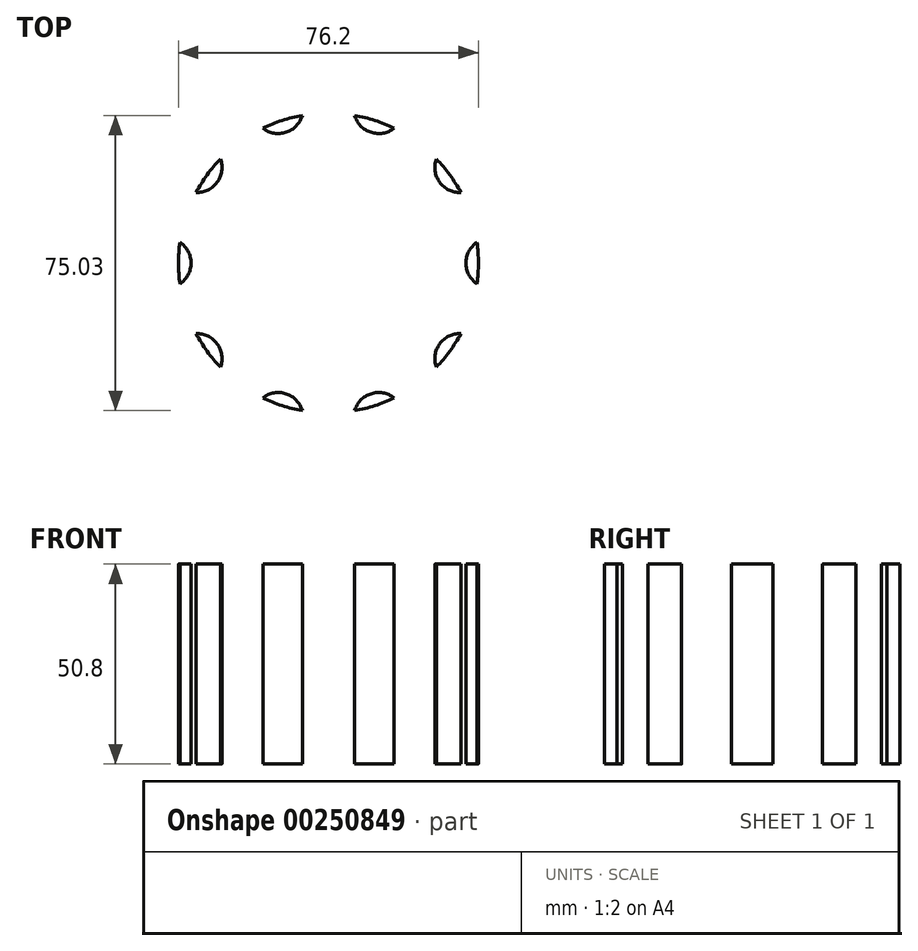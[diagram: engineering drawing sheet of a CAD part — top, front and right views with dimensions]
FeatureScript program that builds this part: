
annotation { "Feature Type Name" : "Feature", "Feature Type Description" : "" }
export const myFeature = defineFeature(function(context is Context, id is Id, definition is map)
    precondition{}
    {
        {
            var Q0;
            Q0=qCreatedBy(makeId("Top.planeOp"),FACE);
            var sketch = newSketch(context, id + "F0", { "sketchPlane" : qUnion([Q0])});
            skCircle(sketch, "E0", {"center": v(-2.67, -0.87) * mm, "radius": 38.1 * mm});
            skCircle(sketch, "E1", {"center": v(38.6, -0.87) * mm, "radius": 6.35 * mm});
            skCircle(sketch, "E2.1.0", {"center": v(30.73, -25.13) * mm, "radius": 6.35 * mm});
            skCircle(sketch, "E2.2.0", {"center": v(10.09, -40.12) * mm, "radius": 6.35 * mm});
            skCircle(sketch, "E2.3.0", {"center": v(-15.42, -40.12) * mm, "radius": 6.35 * mm});
            skCircle(sketch, "E2.4.0", {"center": v(-36.06, -25.13) * mm, "radius": 6.35 * mm});
            skCircle(sketch, "E2.5.0", {"center": v(-43.94, -0.87) * mm, "radius": 6.35 * mm});
            skCircle(sketch, "E2.6.0", {"center": v(-36.06, 23.4) * mm, "radius": 6.35 * mm});
            skCircle(sketch, "E2.7.0", {"center": v(-15.42, 38.39) * mm, "radius": 6.35 * mm});
            skCircle(sketch, "E2.8.0", {"center": v(10.09, 38.39) * mm, "radius": 6.35 * mm});
            skCircle(sketch, "E2.9.0", {"center": v(30.73, 23.4) * mm, "radius": 6.35 * mm});
            skLineSegment(sketch, "E2.anchor1", {"start": v(-2.67, -0.87) * mm, "end": v(38.6, -0.87) * mm, "construction": true});
            skLineSegment(sketch, "E2.anchor2", {"start": v(-2.67, -0.87) * mm, "end": v(30.73, 23.4) * mm, "construction": true});
            skSolve(sketch);
        }
        {
            var Q0;
            {var subQ0=sQuery(id+"F0.wireOp",EDGE,"E2.7.0");var subQ1=sQuery(id+"F0.wireOp",EDGE,"E0");var subQ2=makeQuery(id+"F0.imprint","INTERSECT",VERTEX,{"disambiguationData":[OD(0.0)],"derivedFrom":[subQ1,subQ0]});Q0=makeQuery(id+"F0.imprint","IMPRINT",FACE,{"disambiguationData":[TD([[makeQuery(id+"F0.imprint","IMPRINT",EDGE,{"disambiguationData":[TD([[subQ2,-1.0]])],"derivedFrom":subQ1}),1.0]])]});}
            var Q1;
            {var subQ0=sQuery(id+"F0.wireOp",EDGE,"E2.6.0");var subQ1=sQuery(id+"F0.wireOp",EDGE,"E0");var subQ2=makeQuery(id+"F0.imprint","INTERSECT",VERTEX,{"disambiguationData":[OD(0.0)],"derivedFrom":[subQ1,subQ0]});Q1=makeQuery(id+"F0.imprint","IMPRINT",FACE,{"disambiguationData":[TD([[makeQuery(id+"F0.imprint","IMPRINT",EDGE,{"disambiguationData":[TD([[subQ2,-1.0]])],"derivedFrom":subQ1}),1.0]])]});}
            var Q2;
            {var subQ0=sQuery(id+"F0.wireOp",EDGE,"E2.5.0");var subQ1=sQuery(id+"F0.wireOp",EDGE,"E0");var subQ2=makeQuery(id+"F0.imprint","INTERSECT",VERTEX,{"disambiguationData":[OD(0.0)],"derivedFrom":[subQ1,subQ0]});Q2=makeQuery(id+"F0.imprint","IMPRINT",FACE,{"disambiguationData":[TD([[makeQuery(id+"F0.imprint","IMPRINT",EDGE,{"disambiguationData":[TD([[subQ2,-1.0]])],"derivedFrom":subQ1}),1.0]])]});}
            var Q3;
            {var subQ0=sQuery(id+"F0.wireOp",EDGE,"E2.8.0");var subQ1=sQuery(id+"F0.wireOp",EDGE,"E0");var subQ2=makeQuery(id+"F0.imprint","INTERSECT",VERTEX,{"disambiguationData":[OD(0.0)],"derivedFrom":[subQ1,subQ0]});Q3=makeQuery(id+"F0.imprint","IMPRINT",FACE,{"disambiguationData":[TD([[makeQuery(id+"F0.imprint","IMPRINT",EDGE,{"disambiguationData":[TD([[subQ2,-1.0]])],"derivedFrom":subQ1}),1.0]])]});}
            var Q4;
            {var subQ0=sQuery(id+"F0.wireOp",EDGE,"E2.9.0");var subQ1=sQuery(id+"F0.wireOp",EDGE,"E0");var subQ2=makeQuery(id+"F0.imprint","INTERSECT",VERTEX,{"disambiguationData":[OD(0.0)],"derivedFrom":[subQ1,subQ0]});Q4=makeQuery(id+"F0.imprint","IMPRINT",FACE,{"disambiguationData":[TD([[makeQuery(id+"F0.imprint","IMPRINT",EDGE,{"disambiguationData":[TD([[subQ2,-1.0]])],"derivedFrom":subQ1}),1.0]])]});}
            var Q5;
            {var subQ0=sQuery(id+"F0.wireOp",EDGE,"E1");var subQ1=sQuery(id+"F0.wireOp",EDGE,"E0");var subQ2=makeQuery(id+"F0.imprint","INTERSECT",VERTEX,{"disambiguationData":[OD(0.0)],"derivedFrom":[subQ1,subQ0]});Q5=makeQuery(id+"F0.imprint","IMPRINT",FACE,{"disambiguationData":[TD([[makeQuery(id+"F0.imprint","IMPRINT",EDGE,{"disambiguationData":[TD([[subQ2,1.0]])],"derivedFrom":subQ1}),1.0]])]});}
            var Q6;
            {var subQ0=sQuery(id+"F0.wireOp",EDGE,"E2.1.0");var subQ1=sQuery(id+"F0.wireOp",EDGE,"E0");var subQ2=makeQuery(id+"F0.imprint","INTERSECT",VERTEX,{"disambiguationData":[OD(0.0)],"derivedFrom":[subQ1,subQ0]});Q6=makeQuery(id+"F0.imprint","IMPRINT",FACE,{"disambiguationData":[TD([[makeQuery(id+"F0.imprint","IMPRINT",EDGE,{"disambiguationData":[TD([[subQ2,-1.0]])],"derivedFrom":subQ1}),1.0]])]});}
            var Q7;
            {var subQ0=sQuery(id+"F0.wireOp",EDGE,"E2.2.0");var subQ1=sQuery(id+"F0.wireOp",EDGE,"E0");var subQ2=makeQuery(id+"F0.imprint","INTERSECT",VERTEX,{"disambiguationData":[OD(0.0)],"derivedFrom":[subQ1,subQ0]});Q7=makeQuery(id+"F0.imprint","IMPRINT",FACE,{"disambiguationData":[TD([[makeQuery(id+"F0.imprint","IMPRINT",EDGE,{"disambiguationData":[TD([[subQ2,-1.0]])],"derivedFrom":subQ1}),1.0]])]});}
            var Q8;
            {var subQ0=sQuery(id+"F0.wireOp",EDGE,"E2.3.0");var subQ1=sQuery(id+"F0.wireOp",EDGE,"E0");var subQ2=makeQuery(id+"F0.imprint","INTERSECT",VERTEX,{"disambiguationData":[OD(0.0)],"derivedFrom":[subQ1,subQ0]});Q8=makeQuery(id+"F0.imprint","IMPRINT",FACE,{"disambiguationData":[TD([[makeQuery(id+"F0.imprint","IMPRINT",EDGE,{"disambiguationData":[TD([[subQ2,-1.0]])],"derivedFrom":subQ1}),1.0]])]});}
            var Q9;
            {var subQ0=sQuery(id+"F0.wireOp",EDGE,"E2.4.0");var subQ1=sQuery(id+"F0.wireOp",EDGE,"E0");var subQ2=makeQuery(id+"F0.imprint","INTERSECT",VERTEX,{"disambiguationData":[OD(0.0)],"derivedFrom":[subQ1,subQ0]});Q9=makeQuery(id+"F0.imprint","IMPRINT",FACE,{"disambiguationData":[TD([[makeQuery(id+"F0.imprint","IMPRINT",EDGE,{"disambiguationData":[TD([[subQ2,-1.0]])],"derivedFrom":subQ1}),1.0]])]});}
            extrude(context, id + "F1", {"entities" : qUnion([Q0, Q1, Q2, Q3, Q4, Q5, Q6, Q7, Q8, Q9]), "depth" : 50.8 * mm});
        }
    });
